# Revit family: ROTHOB_Rothoblaas_Plate_VGUPlateT
name_source: partatom
category: Structural Connections
units: mm (PartAtom-declared; Revit-internal decimal feet)

## family parameters
Cut with Voids When Loaded = No
Enable cutting in views = Yes
Host = Face
Material for Model Behavior = Steel
OmniClass Number = 23.13.23.11.19.13
OmniClass Title = Wood Connectors
Shared = No

## types (2) — shared parameters
BBACode = BS EN 14545
BIMObjectName = ROTHOB_Rothoblaas_Plate_VGUPlateT
CECode = EN 14545
Category = Pr_20_29_31_12: Carbon steel nailing plates
CodePerformance = CE - Construction products
Color = Silver
Default Elevation = 1219.2 mm  [stored 4 ft]
Description = Plate for tensile load
DurationUnit = Years
Esporta tipo in formato IFC con nome = IfcDiscreteAccessoryType
ExpectedLife = 50
Features = Perforated plates for structural use on timber support structure
Finish = Zinc plated
IfcExportAs = IfcDiscreteAccessoryType
IfcExportType = USERDEFINED
ManufacturerName = ROTHO BLAAS SRL
ManufacturerURL = www.rothoblaas.com
Material = Carbon steel
ModelDisclaimer = The latest version of the data sheets can be found on our website
Name = Plate
ObjectMaterial = ROTHOB_Rothoblaas_CarbonSteel_ZincPlated
OmniClassCode = 23-13 23 11 19 13
OmniClassTitle = Wood Connectors
OmniClassVersion = 2012-05-16
ProductInformation = https://www.rothoblaas.com
Revision = 1
Shape = Two-dimensional
Tipo IFC predefinito = USERDEFINED
UniClass2015Code = Pr_20_29_31_12
UniClass2015Title = Carbon steel nailing plates
UniClass2015Version = Products v1.33
Version = 2

## per-type parameters (varying)
| type | HasHole_VGUPLATET185 | HasHole_VGUPLATET350 | HoleDistance | Length_L | MinWeight | ModelNumber | ModelNumberCode | NominalLength | NominalWidth | Size | Size_Imperial | Thickness_s | Width_B |
| VGUPLATET185_088x185mm | Yes | No | 7 mm  [stored 0.0229659 ft] | 185 mm  [stored 0.606955 ft] | 0.44 kg | VGUPLATET185 | 185 | 185 mm  [stored 0.606955 ft] | 88 mm  [stored 0.288714 ft] | 88x185 mm | 3 7/16x7 1/4 in | 3 mm  [stored 0.00984252 ft] | 88 mm  [stored 0.288714 ft] |
| VGUPLATET350_108x350mm | No | Yes | 76.5 mm  [stored 0.250984 ft] | 350 mm  [stored 1.14829 ft] | 1.31 kg | VGUPLATET350 | 350 | 350 mm  [stored 1.14829 ft] | 108 mm  [stored 0.354331 ft] | 108x350 mm | 4 1/4x13 3/4 in | 4 mm  [stored 0.0131234 ft] | 108 mm  [stored 0.354331 ft] |

note: [stored X ft] marks values corroborated as IEEE doubles in the binary element streams (Revit-internal decimal feet)
